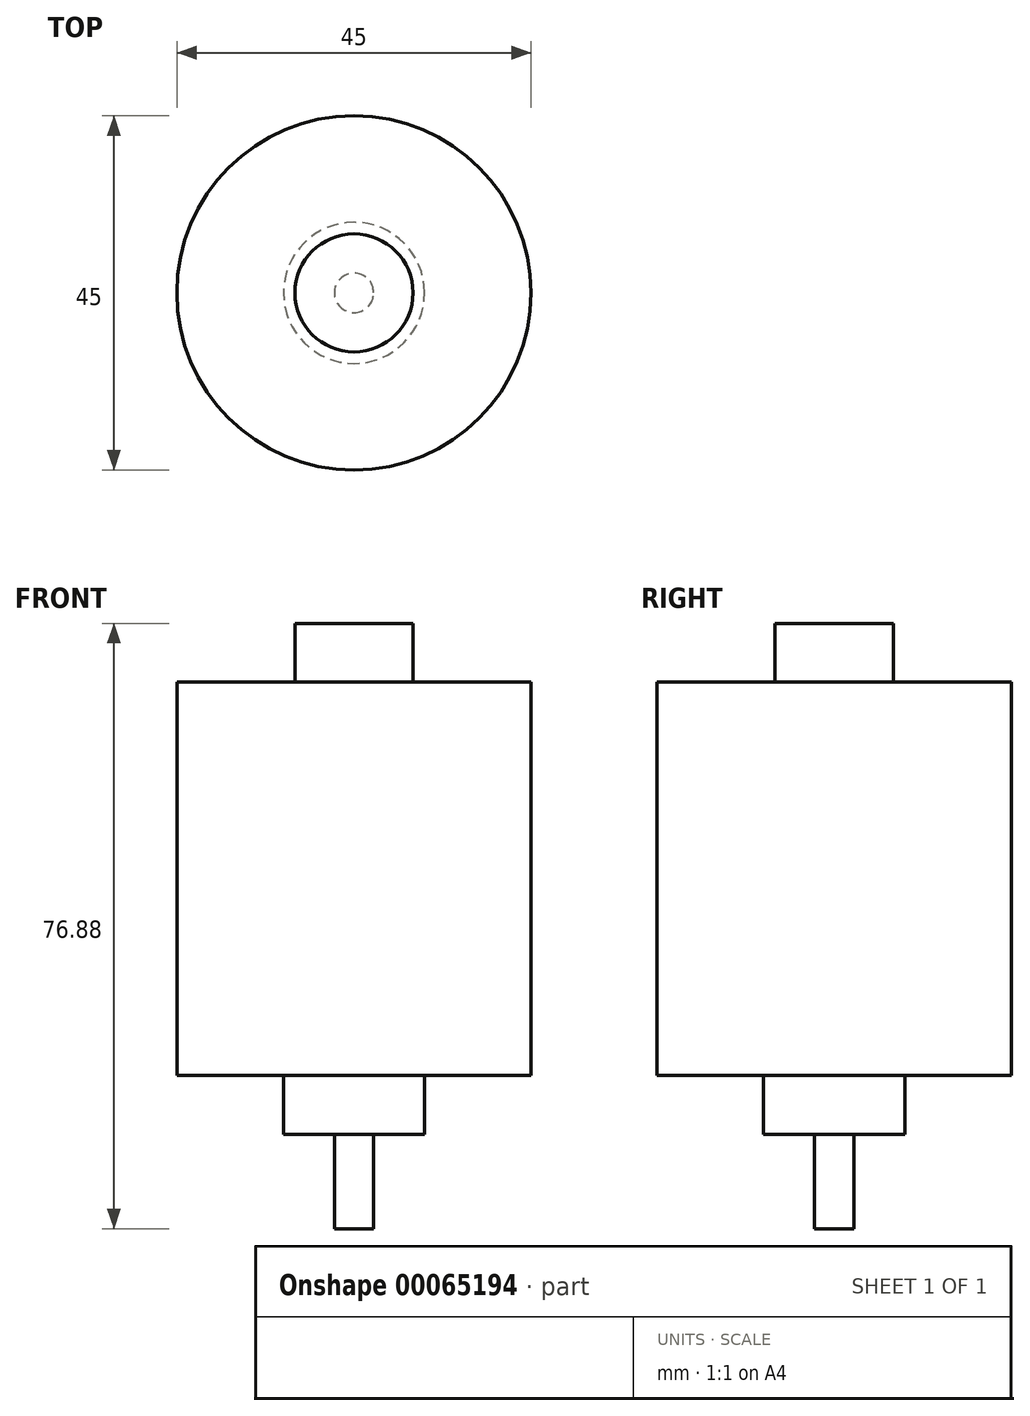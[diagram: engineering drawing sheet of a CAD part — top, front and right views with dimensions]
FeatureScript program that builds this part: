
annotation { "Feature Type Name" : "Feature", "Feature Type Description" : "" }
export const myFeature = defineFeature(function(context is Context, id is Id, definition is map)
    precondition{}
    {
        {
            var Q0;
            Q0=qCreatedBy(makeId("Front.planeOp"),FACE);
            var sketch = newSketch(context, id + "F0", { "sketchPlane" : qUnion([Q0])});
            skLineSegment(sketch, "E0", {"start": v(0, -32.3) * mm, "end": v(-2.5, -32.3) * mm});
            skLineSegment(sketch, "E1", {"start": v(-2.5, -32.3) * mm, "end": v(-2.5, -20.3) * mm});
            skLineSegment(sketch, "E2", {"start": v(-2.5, -20.3) * mm, "end": v(-8.96, -20.3) * mm});
            skLineSegment(sketch, "E3", {"start": v(-8.96, -20.3) * mm, "end": v(-8.96, -12.87) * mm});
            skLineSegment(sketch, "E4", {"start": v(-8.96, -12.87) * mm, "end": v(-22.5, -12.87) * mm});
            skLineSegment(sketch, "E5", {"start": v(-22.5, -12.87) * mm, "end": v(-22.5, 37.13) * mm});
            skLineSegment(sketch, "E6", {"start": v(-22.5, 37.13) * mm, "end": v(-7.5, 37.13) * mm});
            skLineSegment(sketch, "E7", {"start": v(-7.5, 37.13) * mm, "end": v(-7.5, 44.57) * mm});
            skLineSegment(sketch, "E8", {"start": v(-7.5, 44.57) * mm, "end": v(0, 44.57) * mm});
            skLineSegment(sketch, "E9", {"start": v(0, 44.57) * mm, "end": v(0, -32.3) * mm});
            skSolve(sketch);
        }
        {
            var Q0;
            Q0 = qSketchRegion(id + "F0", true);
            var Q1;
            Q1=sQuery(id+"F0.wireOp",EDGE,"E9");
            revolve(context, id + "F1", {"entities" : qUnion([Q0]), "axis" : qUnion([Q1]), "revolveType" : RevolveType.FULL});
        }
    });
